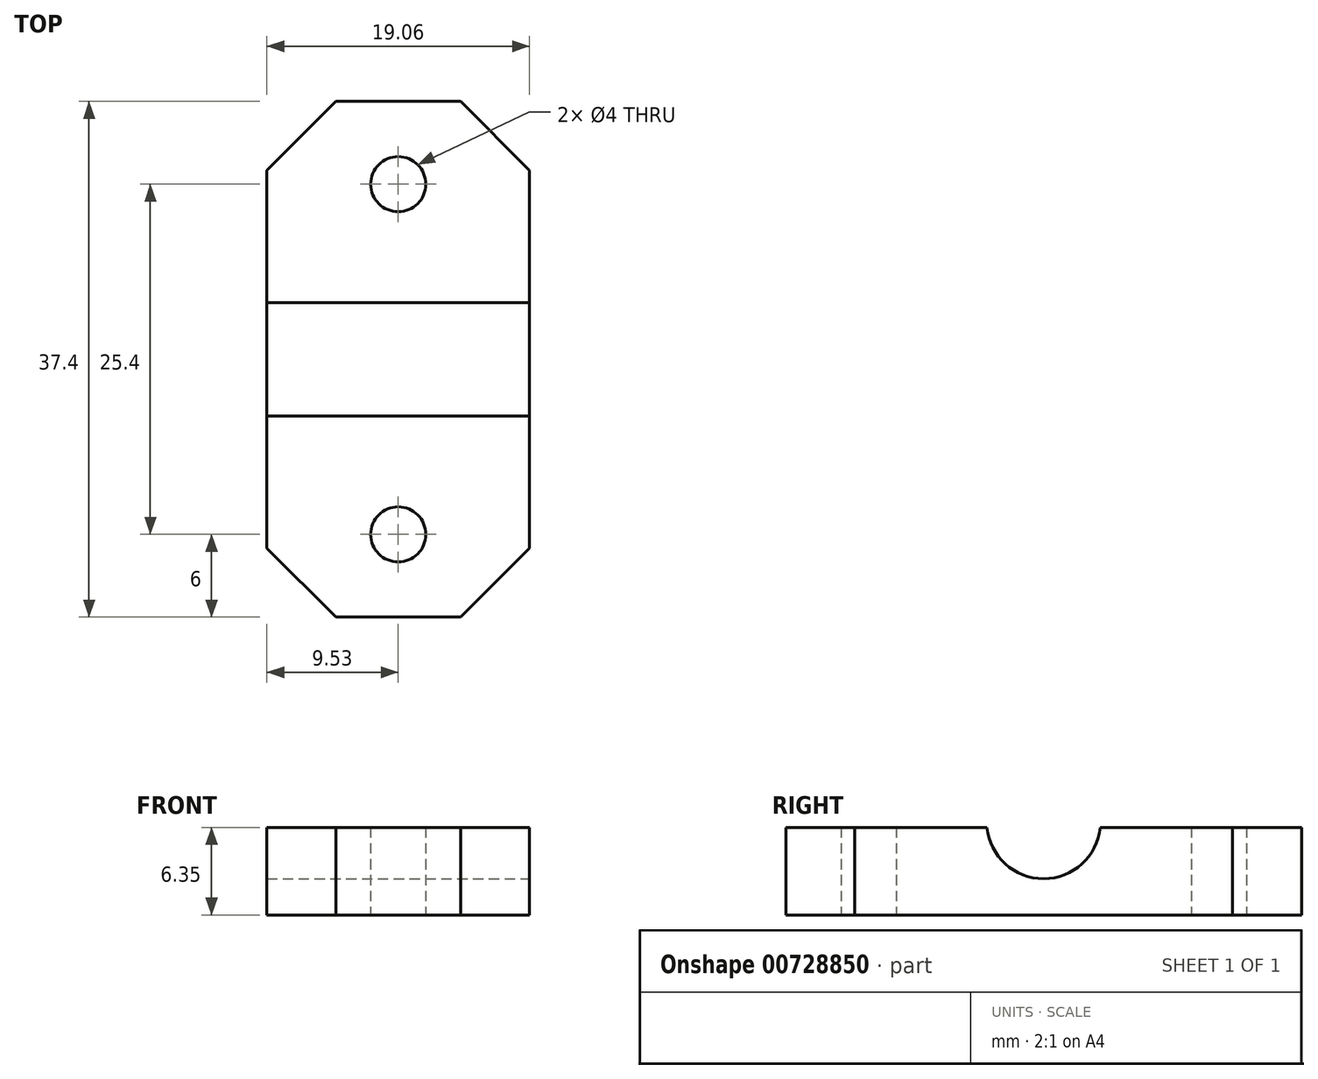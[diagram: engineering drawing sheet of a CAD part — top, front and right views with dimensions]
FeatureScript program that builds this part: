
annotation { "Feature Type Name" : "Feature", "Feature Type Description" : "" }
export const myFeature = defineFeature(function(context is Context, id is Id, definition is map)
    precondition{}
    {
        {
            var Q0;
            Q0=qCreatedBy(makeId("Top.planeOp"),FACE);
            var sketch = newSketch(context, id + "F0", { "sketchPlane" : qUnion([Q0])});
            skLineSegment(sketch, "E0.bottom", {"start": v(-9.53, 18.7) * mm, "end": v(9.52, 18.7) * mm});
            skLineSegment(sketch, "E0.top", {"start": v(-9.53, -18.7) * mm, "end": v(9.53, -18.7) * mm});
            skLineSegment(sketch, "E0.left", {"start": v(-9.53, 18.7) * mm, "end": v(-9.53, -18.7) * mm});
            skLineSegment(sketch, "E0.right", {"start": v(9.52, 18.7) * mm, "end": v(9.52, -18.7) * mm});
            skLineSegment(sketch, "E1", {"start": v(-9.53, 18.7) * mm, "end": v(9.53, -18.7) * mm, "construction": true});
            skCircle(sketch, "E2", {"center": v(0, 12.7) * mm, "radius": 2 * mm});
            skCircle(sketch, "E3", {"center": v(0, -12.7) * mm, "radius": 2 * mm});
            skLineSegment(sketch, "E4", {"start": v(0, -12.7) * mm, "end": v(0, -18.7) * mm, "construction": true});
            skLineSegment(sketch, "E5", {"start": v(0, 12.7) * mm, "end": v(0, 18.7) * mm, "construction": true});
            skSolve(sketch);
        }
        {
            var Q0;
            Q0=makeQuery(id+"F0.imprint","IMPRINT",FACE,{"disambiguationData":[TD([[makeQuery(id+"F0.imprint","IMPRINT",EDGE,{"derivedFrom":sQuery(id+"F0.wireOp",EDGE,"E0.bottom")}),-1.0]])]});
            extrude(context, id + "F1", {"entities" : qUnion([Q0]), "depth" : 6.35 * mm, "offsetDistance" : 25 * mm});
        }
        {
            var Q0;
            Q0=makeQuery(id+"F1.opExtrude","SWEPT_FACE",FACE,{"disambiguationData":[OSD([sQuery(id+"F0.wireOp",EDGE,"E0.right")])]});
            var sketch = newSketch(context, id + "F2", { "sketchPlane" : qUnion([Q0])});
            skCircle(sketch, "E6", {"center": v(0, 6.75) * mm, "radius": 4.13 * mm});
            skSolve(sketch);
        }
        {
            var Q0;
            Q0 = qSketchRegion(id + "F2", true);
            extrude(context, id + "F3", {"entities" : qUnion([Q0]), "operationType" : NewBodyOperationType.REMOVE, "oppositeDirection" : true, "depth" : 100 * mm, "offsetDistance" : 25 * mm});
        }
        {
            var Q0;
            Q0=makeQuery(id+"F1.opExtrude","SWEPT_EDGE",EDGE,{"disambiguationData":[OSD([sQuery(id+"F0.wireOp",EDGE,"E0.top"),sQuery(id+"F0.wireOp",EDGE,"E0.right")])]});
            var Q1;
            Q1=makeQuery(id+"F1.opExtrude","SWEPT_EDGE",EDGE,{"disambiguationData":[OSD([sQuery(id+"F0.wireOp",EDGE,"E0.top"),sQuery(id+"F0.wireOp",EDGE,"E0.left")])]});
            var Q2;
            Q2=makeQuery(id+"F1.opExtrude","SWEPT_EDGE",EDGE,{"disambiguationData":[OSD([sQuery(id+"F0.wireOp",EDGE,"E0.bottom"),sQuery(id+"F0.wireOp",EDGE,"E0.left")])]});
            var Q3;
            Q3=makeQuery(id+"F1.opExtrude","SWEPT_EDGE",EDGE,{"disambiguationData":[OSD([sQuery(id+"F0.wireOp",EDGE,"E0.bottom"),sQuery(id+"F0.wireOp",EDGE,"E0.right")])]});
            chamfer(context, id + "F4", {"entities" : qUnion([Q0, Q1, Q2, Q3]), "width" : 5 * mm, "tangentPropagation" : true});
        }
    });
